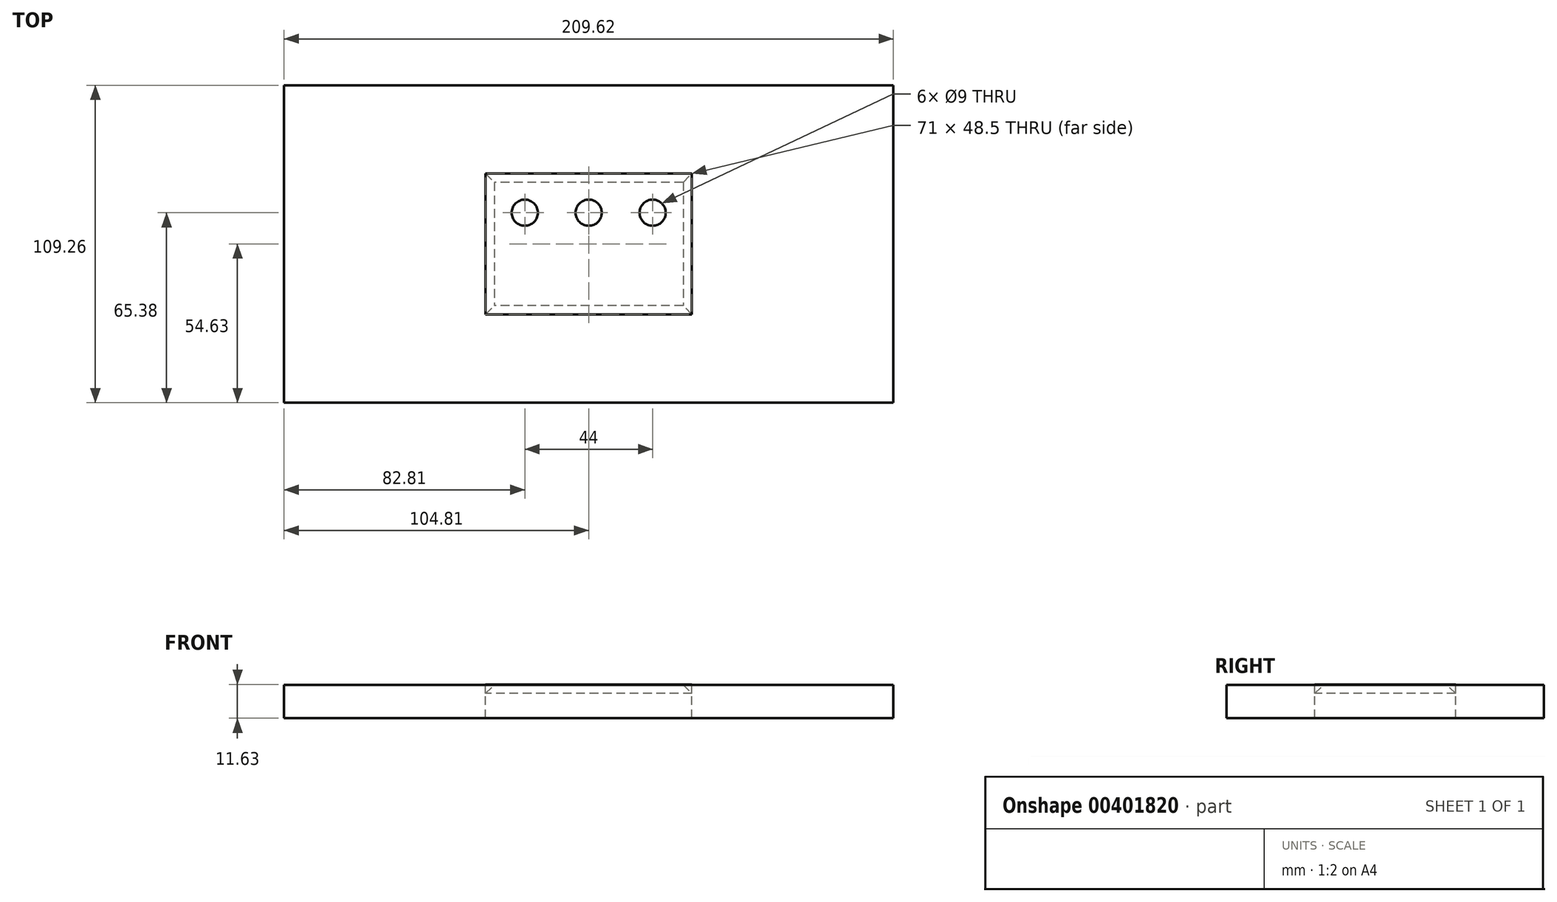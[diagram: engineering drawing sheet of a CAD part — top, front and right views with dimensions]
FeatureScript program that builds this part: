
annotation { "Feature Type Name" : "Feature", "Feature Type Description" : "" }
export const myFeature = defineFeature(function(context is Context, id is Id, definition is map)
    precondition{}
    {
        {
            var Q0;
            Q0=qCreatedBy(makeId("Top.planeOp"),FACE);
            var sketch = newSketch(context, id + "F0", { "sketchPlane" : qUnion([Q0])});
            skLineSegment(sketch, "E0.bottom", {"start": v(35.5, 24.25) * mm, "end": v(-35.5, 24.25) * mm});
            skLineSegment(sketch, "E0.top", {"start": v(35.5, -24.25) * mm, "end": v(-35.5, -24.25) * mm});
            skLineSegment(sketch, "E0.left", {"start": v(35.5, 24.25) * mm, "end": v(35.5, -24.25) * mm});
            skLineSegment(sketch, "E0.right", {"start": v(-35.5, 24.25) * mm, "end": v(-35.5, -24.25) * mm});
            skPoint(sketch, "E0.middle", {"position": v(0, 0) * mm});
            skLineSegment(sketch, "E1", {"start": v(-35.5, -15.25) * mm, "end": v(35.5, -15.25) * mm, "construction": true});
            skLineSegment(sketch, "E2", {"start": v(-35.5, 4.75) * mm, "end": v(35.5, 4.75) * mm, "construction": true});
            skLineSegment(sketch, "E3.bottom", {"start": v(104.81, 54.63) * mm, "end": v(-104.81, 54.63) * mm});
            skLineSegment(sketch, "E3.top", {"start": v(104.81, -54.63) * mm, "end": v(-104.81, -54.63) * mm});
            skLineSegment(sketch, "E3.left", {"start": v(104.81, 54.63) * mm, "end": v(104.81, -54.63) * mm});
            skLineSegment(sketch, "E3.right", {"start": v(-104.81, 54.63) * mm, "end": v(-104.81, -54.63) * mm});
            skLineSegment(sketch, "E4.bottom", {"start": v(32.5, 21.25) * mm, "end": v(-32.5, 21.25) * mm});
            skLineSegment(sketch, "E4.top", {"start": v(32.5, -21.25) * mm, "end": v(-32.5, -21.25) * mm});
            skLineSegment(sketch, "E4.left", {"start": v(32.5, 21.25) * mm, "end": v(32.5, -21.25) * mm});
            skLineSegment(sketch, "E4.right", {"start": v(-32.5, 21.25) * mm, "end": v(-32.5, -21.25) * mm});
            skCircle(sketch, "E5", {"center": v(-22, -10.75) * mm, "radius": 4.5 * mm});
            skCircle(sketch, "E6", {"center": v(0, -10.75) * mm, "radius": 4.5 * mm});
            skCircle(sketch, "E7", {"center": v(22, -10.75) * mm, "radius": 4.5 * mm});
            skLineSegment(sketch, "E8", {"start": v(-22, -10.75) * mm, "end": v(-32.5, -10.75) * mm, "construction": true});
            skLineSegment(sketch, "E9", {"start": v(-22, -10.75) * mm, "end": v(-22, -21.25) * mm, "construction": true});
            skLineSegment(sketch, "E10", {"start": v(22, -10.75) * mm, "end": v(32.5, -10.75) * mm, "construction": true});
            skLineSegment(sketch, "E11", {"start": v(22, -10.75) * mm, "end": v(22, -21.25) * mm, "construction": true});
            skLineSegment(sketch, "E12", {"start": v(0, -21.25) * mm, "end": v(0, -10.75) * mm, "construction": true});
            skLineSegment(sketch, "E13", {"start": v(0, -10.75) * mm, "end": v(-22, -10.75) * mm, "construction": true});
            skLineSegment(sketch, "E14", {"start": v(0, -10.75) * mm, "end": v(22, -10.75) * mm, "construction": true});
            skLineSegment(sketch, "E15", {"start": v(-32.5, 0) * mm, "end": v(32.5, 0) * mm, "construction": true});
            skCircle(sketch, "E16.MirrorC", {"center": v(-22, 10.75) * mm, "radius": 4.5 * mm});
            skCircle(sketch, "E17.MirrorC", {"center": v(0, 10.75) * mm, "radius": 4.5 * mm});
            skCircle(sketch, "E18.MirrorC", {"center": v(22, 10.75) * mm, "radius": 4.5 * mm});
            skSolve(sketch);
        }
        {
            var Q0;
            Q0=makeQuery(id+"F0.imprint","IMPRINT",FACE,{"disambiguationData":[TD([[makeQuery(id+"F0.imprint","IMPRINT",EDGE,{"derivedFrom":sQuery(id+"F0.wireOp",EDGE,"E0.bottom")}),-1.0]])]});
            extrude(context, id + "F1", {"entities" : qUnion([Q0]), "oppositeDirection" : true, "depth" : 11.5 * mm});
        }
        {
            var Q0;
            Q0=makeQuery(id+"F0.imprint","IMPRINT",FACE,{"disambiguationData":[TD([[makeQuery(id+"F0.imprint","IMPRINT",EDGE,{"derivedFrom":sQuery(id+"F0.wireOp",EDGE,"E0.bottom")}),1.0]])]});
            var Q1;
            Q1=makeQuery(id+"F0.imprint","IMPRINT",FACE,{"disambiguationData":[TD([[makeQuery(id+"F0.imprint","IMPRINT",EDGE,{"derivedFrom":sQuery(id+"F0.wireOp",EDGE,"E4.bottom")}),1.0]])]});
            var Q2;
            Q2=makeQuery(id+"F0.imprint","IMPRINT",FACE,{"disambiguationData":[TD([[makeQuery(id+"F0.imprint","IMPRINT",EDGE,{"derivedFrom":sQuery(id+"F0.wireOp",EDGE,"E7")}),1.0]])]});
            var Q3;
            Q3=makeQuery(id+"F0.imprint","IMPRINT",FACE,{"disambiguationData":[TD([[makeQuery(id+"F0.imprint","IMPRINT",EDGE,{"derivedFrom":sQuery(id+"F0.wireOp",EDGE,"E6")}),1.0]])]});
            var Q4;
            Q4=makeQuery(id+"F0.imprint","IMPRINT",FACE,{"disambiguationData":[TD([[makeQuery(id+"F0.imprint","IMPRINT",EDGE,{"derivedFrom":sQuery(id+"F0.wireOp",EDGE,"E5")}),1.0]])]});
            var Q5;
            Q5=makeQuery(id+"F0.imprint","IMPRINT",FACE,{"disambiguationData":[TD([[makeQuery(id+"F0.imprint","IMPRINT",EDGE,{"derivedFrom":sQuery(id+"F0.wireOp",EDGE,"E16.MirrorC")}),-1.0]])]});
            var Q6;
            Q6=makeQuery(id+"F0.imprint","IMPRINT",FACE,{"disambiguationData":[TD([[makeQuery(id+"F0.imprint","IMPRINT",EDGE,{"derivedFrom":sQuery(id+"F0.wireOp",EDGE,"E17.MirrorC")}),-1.0]])]});
            var Q7;
            Q7=makeQuery(id+"F0.imprint","IMPRINT",FACE,{"disambiguationData":[TD([[makeQuery(id+"F0.imprint","IMPRINT",EDGE,{"derivedFrom":sQuery(id+"F0.wireOp",EDGE,"E18.MirrorC")}),-1.0]])]});
            extrude(context, id + "F2", {"entities" : qUnion([Q0, Q1, Q2, Q3, Q4, Q5, Q6, Q7]), "depth" : .125 * mm});
        }
        {
            var Q0;
            Q0=makeQuery(id+"F0.imprint","IMPRINT",FACE,{"disambiguationData":[TD([[makeQuery(id+"F0.imprint","IMPRINT",EDGE,{"derivedFrom":sQuery(id+"F0.wireOp",EDGE,"E0.bottom")}),1.0]])]});
            extrude(context, id + "F3", {"entities" : qUnion([Q0]), "oppositeDirection" : true, "depth" : 3 * mm});
        }
        {
            var Q0;
            Q0=makeQuery(id+"F3.opExtrude","CAP_EDGE",EDGE,{"disambiguationData":[OSD([sQuery(id+"F0.wireOp",EDGE,"E4.left")])],"isStart":false});
            var Q1;
            Q1=makeQuery(id+"F3.opExtrude","CAP_EDGE",EDGE,{"disambiguationData":[OSD([sQuery(id+"F0.wireOp",EDGE,"E4.top")])],"isStart":false});
            var Q2;
            Q2=makeQuery(id+"F3.opExtrude","CAP_EDGE",EDGE,{"disambiguationData":[OSD([sQuery(id+"F0.wireOp",EDGE,"E4.bottom")])],"isStart":false});
            var Q3;
            Q3=makeQuery(id+"F3.opExtrude","CAP_EDGE",EDGE,{"disambiguationData":[OSD([sQuery(id+"F0.wireOp",EDGE,"E4.right")])],"isStart":false});
            chamfer(context, id + "F4", {"entities" : qUnion([Q0, Q1, Q2, Q3]), "width" : 3 * mm, "tangentPropagation" : true});
        }
        {
            var Q0;
            Q0=makeQuery(id+"F0.imprint","IMPRINT",FACE,{"disambiguationData":[TD([[makeQuery(id+"F0.imprint","IMPRINT",EDGE,{"derivedFrom":sQuery(id+"F0.wireOp",EDGE,"E7")}),1.0]])]});
            var Q1;
            Q1=makeQuery(id+"F0.imprint","IMPRINT",FACE,{"disambiguationData":[TD([[makeQuery(id+"F0.imprint","IMPRINT",EDGE,{"derivedFrom":sQuery(id+"F0.wireOp",EDGE,"E18.MirrorC")}),-1.0]])]});
            var Q2;
            Q2=makeQuery(id+"F0.imprint","IMPRINT",FACE,{"disambiguationData":[TD([[makeQuery(id+"F0.imprint","IMPRINT",EDGE,{"derivedFrom":sQuery(id+"F0.wireOp",EDGE,"E17.MirrorC")}),-1.0]])]});
            var Q3;
            Q3=makeQuery(id+"F0.imprint","IMPRINT",FACE,{"disambiguationData":[TD([[makeQuery(id+"F0.imprint","IMPRINT",EDGE,{"derivedFrom":sQuery(id+"F0.wireOp",EDGE,"E6")}),1.0]])]});
            var Q4;
            Q4=makeQuery(id+"F0.imprint","IMPRINT",FACE,{"disambiguationData":[TD([[makeQuery(id+"F0.imprint","IMPRINT",EDGE,{"derivedFrom":sQuery(id+"F0.wireOp",EDGE,"E16.MirrorC")}),-1.0]])]});
            var Q5;
            Q5=makeQuery(id+"F0.imprint","IMPRINT",FACE,{"disambiguationData":[TD([[makeQuery(id+"F0.imprint","IMPRINT",EDGE,{"derivedFrom":sQuery(id+"F0.wireOp",EDGE,"E5")}),1.0]])]});
            extrude(context, id + "F5", {"entities" : qUnion([Q0, Q1, Q2, Q3, Q4, Q5]), "endBound" : BoundingType.SYMMETRIC, "oppositeDirection" : true, "depth" : .125 * mm});
        }
    });
